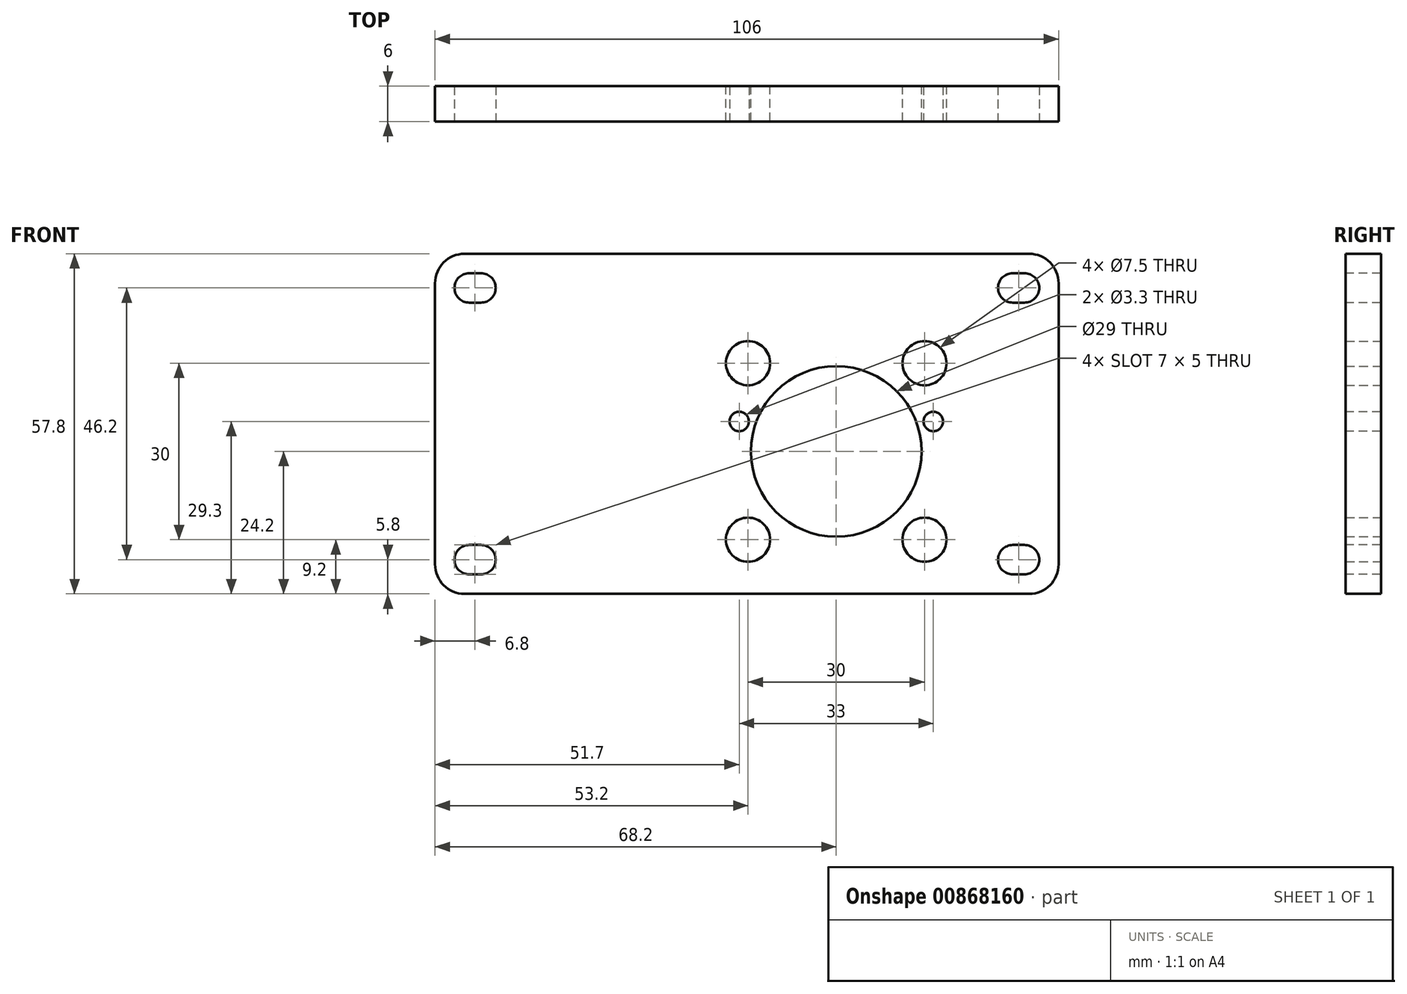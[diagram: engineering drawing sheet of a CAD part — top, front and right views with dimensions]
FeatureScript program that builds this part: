
annotation { "Feature Type Name" : "Feature", "Feature Type Description" : "" }
export const myFeature = defineFeature(function(context is Context, id is Id, definition is map)
    precondition{}
    {
        {
            var Q0;
            Q0=qCreatedBy(makeId("Front.planeOp"),FACE);
            var sketch = newSketch(context, id + "F0", { "sketchPlane" : qUnion([Q0])});
            skLineSegment(sketch, "E0.bottom", {"start": v(0, 0) * mm, "end": v(106, 0) * mm});
            skLineSegment(sketch, "E0.top", {"start": v(0, 57.8) * mm, "end": v(106, 57.8) * mm});
            skLineSegment(sketch, "E0.left", {"start": v(0, 0) * mm, "end": v(0, 57.8) * mm});
            skLineSegment(sketch, "E0.right", {"start": v(106, 0) * mm, "end": v(106, 57.8) * mm});
            skCircle(sketch, "E1", {"center": v(68.2, 24.2) * mm, "radius": 14.5 * mm});
            skLineSegment(sketch, "E2", {"start": v(68.2, -13.24) * mm, "end": v(68.2, 69.39) * mm, "construction": true});
            skLineSegment(sketch, "E3", {"start": v(24.26, 24.2) * mm, "end": v(141.51, 24.2) * mm, "construction": true});
            skCircle(sketch, "E4", {"center": v(53.2, 39.2) * mm, "radius": 3.75 * mm});
            skCircle(sketch, "E5", {"center": v(53.2, 9.2) * mm, "radius": 3.75 * mm});
            skCircle(sketch, "E6", {"center": v(83.2, 9.2) * mm, "radius": 3.75 * mm});
            skCircle(sketch, "E7", {"center": v(83.2, 39.2) * mm, "radius": 3.75 * mm});
            skSolve(sketch);
        }
        {
            var Q0;
            Q0=makeQuery(id+"F0.imprint","IMPRINT",FACE,{"disambiguationData":[TD([[makeQuery(id+"F0.imprint","IMPRINT",EDGE,{"derivedFrom":sQuery(id+"F0.wireOp",EDGE,"E0.bottom")}),1.0]])]});
            extrude(context, id + "F1", {"entities" : qUnion([Q0]), "depth" : 6 * mm, "offsetDistance" : 25 * mm});
        }
        {
            var Q0;
            Q0=makeQuery(id+"F1.opExtrude","CAP_FACE",FACE,{"disambiguationData":[OSD([sQuery(id+"F0.wireOp",EDGE,"E0.bottom"),sQuery(id+"F0.wireOp",EDGE,"E0.top"),sQuery(id+"F0.wireOp",EDGE,"E0.left"),sQuery(id+"F0.wireOp",EDGE,"E0.right"),sQuery(id+"F0.wireOp",EDGE,"E1"),sQuery(id+"F0.wireOp",EDGE,"E4"),sQuery(id+"F0.wireOp",EDGE,"E5"),sQuery(id+"F0.wireOp",EDGE,"E6"),sQuery(id+"F0.wireOp",EDGE,"E7")])],"isStart":false});
            var sketch = newSketch(context, id + "F2", { "sketchPlane" : qUnion([Q0])});
            skArc(sketch, "E8", {"start": v(5.8, 54.5) * mm, "mid": v(3.3, 52) * mm, "end": v(5.8, 49.5) * mm});
            skArc(sketch, "E9", {"start": v(7.8, 49.5) * mm, "mid": v(10.3, 52) * mm, "end": v(7.8, 54.5) * mm});
            skLineSegment(sketch, "E10", {"start": v(5.8, 54.5) * mm, "end": v(7.8, 54.5) * mm});
            skLineSegment(sketch, "E11", {"start": v(5.8, 49.5) * mm, "end": v(7.8, 49.5) * mm});
            skArc(sketch, "E12", {"start": v(5.8, 8.3) * mm, "mid": v(3.3, 5.8) * mm, "end": v(5.8, 3.3) * mm});
            skArc(sketch, "E13", {"start": v(7.8, 3.3) * mm, "mid": v(10.3, 5.8) * mm, "end": v(7.8, 8.3) * mm});
            skLineSegment(sketch, "E14", {"start": v(5.8, 8.3) * mm, "end": v(7.8, 8.3) * mm});
            skLineSegment(sketch, "E15", {"start": v(5.8, 3.3) * mm, "end": v(7.8, 3.3) * mm});
            skArc(sketch, "E16", {"start": v(98.2, 8.3) * mm, "mid": v(95.7, 5.8) * mm, "end": v(98.2, 3.3) * mm});
            skArc(sketch, "E17", {"start": v(100.2, 3.3) * mm, "mid": v(102.7, 5.8) * mm, "end": v(100.2, 8.3) * mm});
            skLineSegment(sketch, "E18", {"start": v(98.2, 8.3) * mm, "end": v(100.2, 8.3) * mm});
            skLineSegment(sketch, "E19", {"start": v(98.2, 3.3) * mm, "end": v(100.2, 3.3) * mm});
            skArc(sketch, "E20", {"start": v(98.2, 54.5) * mm, "mid": v(95.7, 52) * mm, "end": v(98.2, 49.5) * mm});
            skArc(sketch, "E21", {"start": v(100.2, 49.5) * mm, "mid": v(102.7, 52) * mm, "end": v(100.2, 54.5) * mm});
            skLineSegment(sketch, "E22", {"start": v(98.2, 54.5) * mm, "end": v(100.2, 54.5) * mm});
            skLineSegment(sketch, "E23", {"start": v(98.2, 49.5) * mm, "end": v(100.2, 49.5) * mm});
            skPoint(sketch, "E24", {"position": v(51.7, 29.3) * mm});
            skPoint(sketch, "E25", {"position": v(84.7, 29.3) * mm});
            skLineSegment(sketch, "E26", {"start": v(68.2, 24.2) * mm, "end": v(68.2, 0) * mm});
            skLineSegment(sketch, "E27", {"start": v(68.2, 0) * mm, "end": v(68.2, 64.15) * mm, "construction": true});
            skLineSegment(sketch, "E28", {"start": v(42.06, 29.3) * mm, "end": v(94.68, 29.3) * mm});
            skSolve(sketch);
        }
        {
            var Q0;
            Q0 = qSketchRegion(id + "F2", true);
            extrude(context, id + "F3", {"entities" : qUnion([Q0]), "operationType" : NewBodyOperationType.REMOVE, "endBound" : BoundingType.UP_TO_NEXT, "oppositeDirection" : true, "depth" : 25 * mm, "offsetDistance" : 25 * mm});
        }
        {
            var Q0;
            Q0=sQuery(id+"F2.wireOp",VERTEX,"E24");
            var Q1;
            Q1=sQuery(id+"F2.wireOp",VERTEX,"E25");
            var Q2;
            Q2=makeQuery(id+"F1.opExtrude","SWEPT_BODY",BODY,{"disambiguationData":[OSD([sQuery(id+"F0.wireOp",EDGE,"E0.bottom"),sQuery(id+"F0.wireOp",EDGE,"E0.top"),sQuery(id+"F0.wireOp",EDGE,"E0.left"),sQuery(id+"F0.wireOp",EDGE,"E0.right"),sQuery(id+"F0.wireOp",EDGE,"E1"),sQuery(id+"F0.wireOp",EDGE,"E4"),sQuery(id+"F0.wireOp",EDGE,"E5"),sQuery(id+"F0.wireOp",EDGE,"E6"),sQuery(id+"F0.wireOp",EDGE,"E7")])]});
            hole(context, id + "F4", {"style" : HoleStyle.SIMPLE, "endStyle" : HoleEndStyle.THROUGH, "standardTappedOrClearance" : lookupTablePath({ "standard" : "ISO", "engagement" : "75%", "pitch" : "0.7 mm", "size" : "M4", "type" : "Tapped" }), "standardBlindInLast" : lookupTablePath({ "standard" : "ISO", "engagement" : "75%", "pitch" : "0.7 mm", "size" : "M4", "type" : "Tapped" }), "holeDiameter" : 3.3 * mm, "majorDiameter" : 4 * mm, "showTappedDepth" : true, "isTappedThrough" : true, "tappedDepth" : 6 * mm, "tapClearance" : 3, "locations" : qUnion([Q0, Q1]), "scope" : qUnion([Q2])});
        }
        {
            var Q0;
            Q0=makeQuery(id+"F1.opExtrude","SWEPT_EDGE",EDGE,{"disambiguationData":[OSD([sQuery(id+"F0.wireOp",EDGE,"E0.top"),sQuery(id+"F0.wireOp",EDGE,"E0.right")])]});
            var Q1;
            Q1=makeQuery(id+"F1.opExtrude","SWEPT_EDGE",EDGE,{"disambiguationData":[OSD([sQuery(id+"F0.wireOp",EDGE,"E0.bottom"),sQuery(id+"F0.wireOp",EDGE,"E0.right")])]});
            var Q2;
            Q2=makeQuery(id+"F1.opExtrude","SWEPT_EDGE",EDGE,{"disambiguationData":[OSD([sQuery(id+"F0.wireOp",EDGE,"E0.bottom"),sQuery(id+"F0.wireOp",EDGE,"E0.left")])]});
            var Q3;
            Q3=makeQuery(id+"F1.opExtrude","SWEPT_EDGE",EDGE,{"disambiguationData":[OSD([sQuery(id+"F0.wireOp",EDGE,"E0.top"),sQuery(id+"F0.wireOp",EDGE,"E0.left")])]});
            fillet(context, id + "F5", {"entities" : qUnion([Q0, Q1, Q2, Q3]), "radius" : 5 * mm, "tangentPropagation" : true, "allowEdgeOverflow" : false});
        }
    });
